# Revit family: Furniture_Office-Chairs_Flokk_Giroflex-353_Visit-Armrests
name_source: partatom
category: Furniture
units: mm (PartAtom-declared; Revit-internal decimal feet)

## family parameters
Always vertical = Yes
Cut with Voids When Loaded = No
OmniClass Number = 23.40.20.14.14.11
OmniClass Title = Chairs
Room Calculation Point = No
Shared = No
Work Plane-Based = No

## types (1)
- Giroflex 353 visit, armrests
    AssetType = Movable
    BIMObjectName = Furniture_Office-Chairs_Flokk_Giroflex-353_Visit-Armrests
    Brand = Flokk
    Category = Giroflex
    Color = Various
    Cost = 0 $
    Default Elevation = 0 mm  [stored 0 ft]
    Description = Refreshingly comfortable and doesn't make a fuss. The giroflex 353 visitor's chair is popular for sitting on.
    DurationUnit = Year
    HighestSeatingHeight = 500 mm  [stored 1.64042 ft]
    IfcExportAs = IfcFurnishingElementType
    IfcExportType = CHAIR
    LowestSeatingHeight = 500 mm  [stored 1.64042 ft]
    MainColor = Various
    Manufacturer = Flokk
    ManufacturerName = Flokk
    ManufacturerURL = https://www.flokk.com
    Material = Plastic, Metal and Textile
    Model = Giroflex 353 visit, armrests
    ModelNumber = 353-3003
    NBSDescription = Stacking chairs
    NBSReference = 45-35-20/355
    Name = Giroflex-353_Visit-Armrests
    NominalDepth = 565 mm
    NominalHeight = 970 mm
    NominalLength = 646 mm
    OfficeChairQuaternaryMaterial = Black RAL 9005
    ProductDatasheet = https://flokkplatformprod.blob.core.windows.net
    ProductInformation = Refreshingly comfortable and doesn't make a fuss. The giroflex 353 visitor's chair is popular for sitting on.
    SeatingHeight = 500 mm  [stored 1.64042 ft]
    Shape = Sculptured
    Size = 650x565x970 mm
    URL = https://store.flokk.com
    Uniclass2 = Pr_40_50_12_51
    Uniclass2015Description = Meeting room chairs
    Uniclass2015Reference = Pr_40_50_12_51
    Version = 1
    VersionDate = 27/12/2022
    WarrantyDurationUnit = Year

note: [stored X ft] marks values corroborated as IEEE doubles in the binary element streams (Revit-internal decimal feet)

## geometry (parser evidence)
native form markers: Sweep x5
no freeform markers — native parametric forms only
